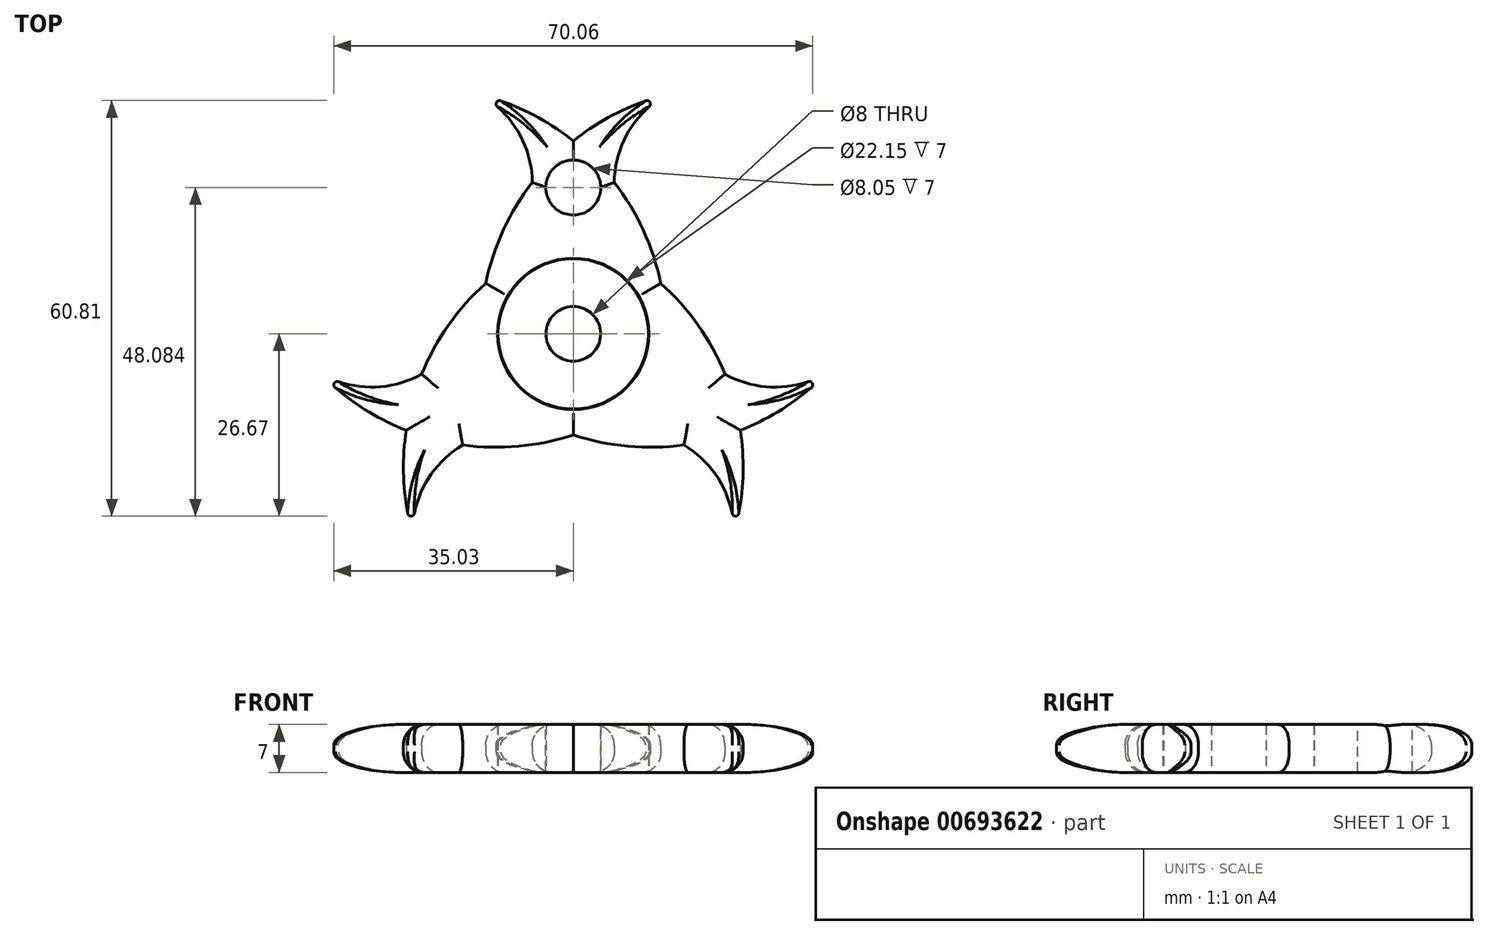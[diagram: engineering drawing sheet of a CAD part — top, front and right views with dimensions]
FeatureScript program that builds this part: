
annotation { "Feature Type Name" : "Feature", "Feature Type Description" : "" }
export const myFeature = defineFeature(function(context is Context, id is Id, definition is map)
    precondition{}
    {
        {
            var Q0;
            Q0=qCreatedBy(makeId("Top.planeOp"),FACE);
            var sketch = newSketch(context, id + "F0", { "sketchPlane" : qUnion([Q0])});
            skCircle(sketch, "E0", {"center": v(0, 0) * mm, "radius": 11.07 * mm});
            skLineSegment(sketch, "E1.bottom", {"start": v(-13.58, 0) * mm, "end": v(13.58, 0) * mm, "construction": true});
            skLineSegment(sketch, "E1.top", {"start": v(-13.58, 35) * mm, "end": v(13.57, 35) * mm, "construction": true});
            skLineSegment(sketch, "E1.left", {"start": v(-13.58, 0) * mm, "end": v(-13.58, 35) * mm, "construction": true});
            skLineSegment(sketch, "E1.right", {"start": v(13.58, 0) * mm, "end": v(13.57, 35) * mm, "construction": true});
            skArc(sketch, "E2", {"start": v(12.81, 7.4) * mm, "mid": v(10.24, 15.16) * mm, "end": v(6, 22.15) * mm});
            skArc(sketch, "E3", {"start": v(13.57, 35) * mm, "mid": v(6.43, 32.33) * mm, "end": v(0, 28.23) * mm});
            skArc(sketch, "E4", {"start": v(-6, 22.15) * mm, "mid": v(-8.07, 29.58) * mm, "end": v(-13.58, 35) * mm});
            skArc(sketch, "E5", {"start": v(13.57, 35) * mm, "mid": v(8.07, 29.58) * mm, "end": v(6, 22.15) * mm});
            skArc(sketch, "E6.trimOffspring", {"start": v(-6, 22.15) * mm, "mid": v(-10.24, 15.16) * mm, "end": v(-12.81, 7.4) * mm});
            skArc(sketch, "E7.trimOffspring", {"start": v(0, 28.23) * mm, "mid": v(-6.43, 32.33) * mm, "end": v(-13.58, 35) * mm});
            skLineSegment(sketch, "E8", {"start": v(0, 28.23) * mm, "end": v(0, 13.58) * mm, "construction": true});
            skArc(sketch, "E9.1.0", {"start": v(-24.45, -14.11) * mm, "mid": v(-24.79, -21.73) * mm, "end": v(-23.52, -29.26) * mm});
            skArc(sketch, "E9.1.1", {"start": v(-16.18, -16.26) * mm, "mid": v(-21.58, -21.78) * mm, "end": v(-23.52, -29.26) * mm});
            skArc(sketch, "E9.1.2", {"start": v(-37.1, -5.74) * mm, "mid": v(-31.22, -10.6) * mm, "end": v(-24.45, -14.11) * mm});
            skArc(sketch, "E9.1.3", {"start": v(-37.1, -5.74) * mm, "mid": v(-29.66, -7.8) * mm, "end": v(-22.18, -5.88) * mm});
            skArc(sketch, "E9.1.4", {"start": v(-12.81, 7.4) * mm, "mid": v(-18.25, 1.29) * mm, "end": v(-22.18, -5.88) * mm});
            skArc(sketch, "E9.1.5", {"start": v(-16.18, -16.26) * mm, "mid": v(-8, -16.45) * mm, "end": v(0, -14.8) * mm});
            skArc(sketch, "E9.2.0", {"start": v(24.45, -14.11) * mm, "mid": v(31.22, -10.6) * mm, "end": v(37.1, -5.74) * mm});
            skArc(sketch, "E9.2.1", {"start": v(22.18, -5.88) * mm, "mid": v(29.66, -7.8) * mm, "end": v(37.1, -5.74) * mm});
            skArc(sketch, "E9.2.2", {"start": v(23.52, -29.26) * mm, "mid": v(24.79, -21.73) * mm, "end": v(24.45, -14.11) * mm});
            skArc(sketch, "E9.2.3", {"start": v(23.52, -29.26) * mm, "mid": v(21.58, -21.78) * mm, "end": v(16.18, -16.26) * mm});
            skArc(sketch, "E9.2.4", {"start": v(0, -14.8) * mm, "mid": v(8, -16.45) * mm, "end": v(16.18, -16.26) * mm});
            skArc(sketch, "E9.2.5", {"start": v(22.18, -5.88) * mm, "mid": v(18.25, 1.29) * mm, "end": v(12.81, 7.4) * mm});
            skPoint(sketch, "E10.orphan", {"position": v(-6.79, 11.76) * mm});
            skPoint(sketch, "E11.orphan", {"position": v(6.79, 11.76) * mm});
            skPoint(sketch, "E12.orphan", {"position": v(6.79, -11.76) * mm});
            skPoint(sketch, "E13.orphan", {"position": v(-6.79, -11.76) * mm});
            skSolve(sketch);
        }
        {
            var Q0;
            Q0 = qSketchRegion(id + "F0", true);
            extrude(context, id + "F1", {"entities" : qUnion([Q0]), "depth" : 7 * mm, "offsetDistance" : 25 * mm});
        }
        {
            var Q0;
            Q0=makeQuery(id+"F1.opExtrude","CAP_EDGE",EDGE,{"disambiguationData":[OSD([sQuery(id+"F0.wireOp",EDGE,"E9.2.5")])],"isStart":false});
            var Q1;
            Q1=makeQuery(id+"F1.opExtrude","CAP_EDGE",EDGE,{"disambiguationData":[OSD([sQuery(id+"F0.wireOp",EDGE,"E2")])],"isStart":false});
            var Q2;
            Q2=makeQuery(id+"F1.opExtrude","CAP_EDGE",EDGE,{"disambiguationData":[OSD([sQuery(id+"F0.wireOp",EDGE,"E5")])],"isStart":false});
            var Q3;
            Q3=makeQuery(id+"F1.opExtrude","CAP_EDGE",EDGE,{"disambiguationData":[OSD([sQuery(id+"F0.wireOp",EDGE,"E3")])],"isStart":false});
            var Q4;
            Q4=makeQuery(id+"F1.opExtrude","CAP_EDGE",EDGE,{"disambiguationData":[OSD([sQuery(id+"F0.wireOp",EDGE,"E7.trimOffspring")])],"isStart":false});
            var Q5;
            Q5=makeQuery(id+"F1.opExtrude","CAP_EDGE",EDGE,{"disambiguationData":[OSD([sQuery(id+"F0.wireOp",EDGE,"E4")])],"isStart":false});
            var Q6;
            Q6=makeQuery(id+"F1.opExtrude","CAP_EDGE",EDGE,{"disambiguationData":[OSD([sQuery(id+"F0.wireOp",EDGE,"E6.trimOffspring")])],"isStart":false});
            var Q7;
            Q7=makeQuery(id+"F1.opExtrude","CAP_EDGE",EDGE,{"disambiguationData":[OSD([sQuery(id+"F0.wireOp",EDGE,"E9.1.4")])],"isStart":false});
            var Q8;
            Q8=makeQuery(id+"F1.opExtrude","CAP_EDGE",EDGE,{"disambiguationData":[OSD([sQuery(id+"F0.wireOp",EDGE,"E9.1.3")])],"isStart":false});
            var Q9;
            Q9=makeQuery(id+"F1.opExtrude","CAP_EDGE",EDGE,{"disambiguationData":[OSD([sQuery(id+"F0.wireOp",EDGE,"E9.1.2")])],"isStart":false});
            var Q10;
            Q10=makeQuery(id+"F1.opExtrude","CAP_EDGE",EDGE,{"disambiguationData":[OSD([sQuery(id+"F0.wireOp",EDGE,"E9.1.0")])],"isStart":true});
            var Q11;
            Q11=makeQuery(id+"F1.opExtrude","CAP_EDGE",EDGE,{"disambiguationData":[OSD([sQuery(id+"F0.wireOp",EDGE,"E9.1.0")])],"isStart":false});
            var Q12;
            Q12=makeQuery(id+"F1.opExtrude","CAP_EDGE",EDGE,{"disambiguationData":[OSD([sQuery(id+"F0.wireOp",EDGE,"E9.1.1")])],"isStart":false});
            var Q13;
            Q13=makeQuery(id+"F1.opExtrude","CAP_EDGE",EDGE,{"disambiguationData":[OSD([sQuery(id+"F0.wireOp",EDGE,"E9.1.5")])],"isStart":false});
            var Q14;
            Q14=makeQuery(id+"F1.opExtrude","CAP_EDGE",EDGE,{"disambiguationData":[OSD([sQuery(id+"F0.wireOp",EDGE,"E9.2.0")])],"isStart":false});
            var Q15;
            Q15=makeQuery(id+"F1.opExtrude","CAP_EDGE",EDGE,{"disambiguationData":[OSD([sQuery(id+"F0.wireOp",EDGE,"E9.2.2")])],"isStart":false});
            var Q16;
            Q16=makeQuery(id+"F1.opExtrude","CAP_EDGE",EDGE,{"disambiguationData":[OSD([sQuery(id+"F0.wireOp",EDGE,"E9.2.3")])],"isStart":false});
            var Q17;
            Q17=makeQuery(id+"F1.opExtrude","CAP_EDGE",EDGE,{"disambiguationData":[OSD([sQuery(id+"F0.wireOp",EDGE,"E9.2.4")])],"isStart":false});
            var Q18;
            Q18=makeQuery(id+"F1.opExtrude","CAP_EDGE",EDGE,{"disambiguationData":[OSD([sQuery(id+"F0.wireOp",EDGE,"E9.2.1")])],"isStart":false});
            var Q19;
            Q19=makeQuery(id+"F1.opExtrude","CAP_EDGE",EDGE,{"disambiguationData":[OSD([sQuery(id+"F0.wireOp",EDGE,"E9.2.0")])],"isStart":true});
            var Q20;
            Q20=makeQuery(id+"F1.opExtrude","CAP_EDGE",EDGE,{"disambiguationData":[OSD([sQuery(id+"F0.wireOp",EDGE,"E9.2.2")])],"isStart":true});
            var Q21;
            Q21=makeQuery(id+"F1.opExtrude","CAP_EDGE",EDGE,{"disambiguationData":[OSD([sQuery(id+"F0.wireOp",EDGE,"E9.2.1")])],"isStart":true});
            var Q22;
            Q22=makeQuery(id+"F1.opExtrude","CAP_EDGE",EDGE,{"disambiguationData":[OSD([sQuery(id+"F0.wireOp",EDGE,"E9.2.5")])],"isStart":true});
            var Q23;
            Q23=makeQuery(id+"F1.opExtrude","CAP_EDGE",EDGE,{"disambiguationData":[OSD([sQuery(id+"F0.wireOp",EDGE,"E2")])],"isStart":true});
            var Q24;
            Q24=makeQuery(id+"F1.opExtrude","CAP_EDGE",EDGE,{"disambiguationData":[OSD([sQuery(id+"F0.wireOp",EDGE,"E5")])],"isStart":true});
            var Q25;
            Q25=makeQuery(id+"F1.opExtrude","CAP_EDGE",EDGE,{"disambiguationData":[OSD([sQuery(id+"F0.wireOp",EDGE,"E3")])],"isStart":true});
            var Q26;
            Q26=makeQuery(id+"F1.opExtrude","CAP_EDGE",EDGE,{"disambiguationData":[OSD([sQuery(id+"F0.wireOp",EDGE,"E7.trimOffspring")])],"isStart":true});
            var Q27;
            Q27=makeQuery(id+"F1.opExtrude","CAP_EDGE",EDGE,{"disambiguationData":[OSD([sQuery(id+"F0.wireOp",EDGE,"E4")])],"isStart":true});
            var Q28;
            Q28=makeQuery(id+"F1.opExtrude","CAP_EDGE",EDGE,{"disambiguationData":[OSD([sQuery(id+"F0.wireOp",EDGE,"E6.trimOffspring")])],"isStart":true});
            var Q29;
            Q29=makeQuery(id+"F1.opExtrude","CAP_EDGE",EDGE,{"disambiguationData":[OSD([sQuery(id+"F0.wireOp",EDGE,"E9.1.4")])],"isStart":true});
            var Q30;
            Q30=makeQuery(id+"F1.opExtrude","CAP_EDGE",EDGE,{"disambiguationData":[OSD([sQuery(id+"F0.wireOp",EDGE,"E9.1.3")])],"isStart":true});
            var Q31;
            Q31=makeQuery(id+"F1.opExtrude","CAP_EDGE",EDGE,{"disambiguationData":[OSD([sQuery(id+"F0.wireOp",EDGE,"E9.1.2")])],"isStart":true});
            var Q32;
            Q32=makeQuery(id+"F1.opExtrude","CAP_EDGE",EDGE,{"disambiguationData":[OSD([sQuery(id+"F0.wireOp",EDGE,"E9.1.1")])],"isStart":true});
            var Q33;
            Q33=makeQuery(id+"F1.opExtrude","CAP_EDGE",EDGE,{"disambiguationData":[OSD([sQuery(id+"F0.wireOp",EDGE,"E9.1.5")])],"isStart":true});
            var Q34;
            Q34=makeQuery(id+"F1.opExtrude","CAP_EDGE",EDGE,{"disambiguationData":[OSD([sQuery(id+"F0.wireOp",EDGE,"E9.2.4")])],"isStart":true});
            var Q35;
            Q35=makeQuery(id+"F1.opExtrude","CAP_EDGE",EDGE,{"disambiguationData":[OSD([sQuery(id+"F0.wireOp",EDGE,"E9.2.3")])],"isStart":true});
            fillet(context, id + "F2", {"entities" : qUnion([Q0, Q1, Q2, Q3, Q4, Q5, Q6, Q7, Q8, Q9, Q10, Q11, Q12, Q13, Q14, Q15, Q16, Q17, Q18, Q19, Q20, Q21, Q22, Q23, Q24, Q25, Q26, Q27, Q28, Q29, Q30, Q31, Q32, Q33, Q34, Q35]), "radius" : 3 * mm, "tangentPropagation" : true, "allowEdgeOverflow" : false});
        }
        {
            var Q0;
            Q0=makeQuery(id+"F1.opExtrude","SWEPT_EDGE",EDGE,{"disambiguationData":[OSD([sQuery(id+"F0.wireOp",EDGE,"E9.1.2"),sQuery(id+"F0.wireOp",EDGE,"E9.1.3")])]});
            var Q1;
            Q1=makeQuery(id+"F1.opExtrude","SWEPT_EDGE",EDGE,{"disambiguationData":[OSD([sQuery(id+"F0.wireOp",EDGE,"E9.1.0"),sQuery(id+"F0.wireOp",EDGE,"E9.1.1")])]});
            var Q2;
            Q2=makeQuery(id+"F1.opExtrude","SWEPT_EDGE",EDGE,{"disambiguationData":[OSD([sQuery(id+"F0.wireOp",EDGE,"E9.2.2"),sQuery(id+"F0.wireOp",EDGE,"E9.2.3")])]});
            var Q3;
            Q3=makeQuery(id+"F1.opExtrude","SWEPT_EDGE",EDGE,{"disambiguationData":[OSD([sQuery(id+"F0.wireOp",EDGE,"E9.2.0"),sQuery(id+"F0.wireOp",EDGE,"E9.2.1")])]});
            var Q4;
            Q4=makeQuery(id+"F1.opExtrude","SWEPT_EDGE",EDGE,{"disambiguationData":[OSD([sQuery(id+"F0.wireOp",EDGE,"E3"),sQuery(id+"F0.wireOp",EDGE,"E5")])]});
            var Q5;
            Q5=makeQuery(id+"F1.opExtrude","SWEPT_EDGE",EDGE,{"disambiguationData":[OSD([sQuery(id+"F0.wireOp",EDGE,"E4"),sQuery(id+"F0.wireOp",EDGE,"E7.trimOffspring")])]});
            fillet(context, id + "F3", {"entities" : qUnion([Q0, Q1, Q2, Q3, Q4, Q5]), "radius" : 0.5 * mm, "tangentPropagation" : true, "allowEdgeOverflow" : false});
        }
        {
            var Q0;
            Q0=makeQuery(id+"F1.opExtrude","CAP_FACE",FACE,{"disambiguationData":[OSD([sQuery(id+"F0.wireOp",EDGE,"E0"),sQuery(id+"F0.wireOp",EDGE,"E2"),sQuery(id+"F0.wireOp",EDGE,"E3"),sQuery(id+"F0.wireOp",EDGE,"E4"),sQuery(id+"F0.wireOp",EDGE,"E5"),sQuery(id+"F0.wireOp",EDGE,"E6.trimOffspring"),sQuery(id+"F0.wireOp",EDGE,"E7.trimOffspring"),sQuery(id+"F0.wireOp",EDGE,"E9.1.0"),sQuery(id+"F0.wireOp",EDGE,"E9.1.1"),sQuery(id+"F0.wireOp",EDGE,"E9.1.2"),sQuery(id+"F0.wireOp",EDGE,"E9.1.3"),sQuery(id+"F0.wireOp",EDGE,"E9.1.4"),sQuery(id+"F0.wireOp",EDGE,"E9.1.5"),sQuery(id+"F0.wireOp",EDGE,"E9.2.0"),sQuery(id+"F0.wireOp",EDGE,"E9.2.1"),sQuery(id+"F0.wireOp",EDGE,"E9.2.2"),sQuery(id+"F0.wireOp",EDGE,"E9.2.3"),sQuery(id+"F0.wireOp",EDGE,"E9.2.4"),sQuery(id+"F0.wireOp",EDGE,"E9.2.5")])],"isStart":false});
            var sketch = newSketch(context, id + "F4", { "sketchPlane" : qUnion([Q0])});
            skLineSegment(sketch, "E14", {"start": v(-3.8, 27.32) * mm, "end": v(10.06, 5.8) * mm, "construction": true});
            skLineSegment(sketch, "E15", {"start": v(-10.06, 5.8) * mm, "end": v(3.8, 27.32) * mm, "construction": true});
            skPoint(sketch, "E16", {"position": v(0, 21.41) * mm});
            skSolve(sketch);
        }
        {
            var Q0;
            Q0=sQuery(id+"F4.wireOp",VERTEX,"E16");
            var Q1;
            Q1=makeQuery(id+"F1.opExtrude","SWEPT_BODY",BODY,{"disambiguationData":[OSD([sQuery(id+"F0.wireOp",EDGE,"E0"),sQuery(id+"F0.wireOp",EDGE,"E2"),sQuery(id+"F0.wireOp",EDGE,"E3"),sQuery(id+"F0.wireOp",EDGE,"E4"),sQuery(id+"F0.wireOp",EDGE,"E5"),sQuery(id+"F0.wireOp",EDGE,"E6.trimOffspring"),sQuery(id+"F0.wireOp",EDGE,"E7.trimOffspring"),sQuery(id+"F0.wireOp",EDGE,"E9.1.0"),sQuery(id+"F0.wireOp",EDGE,"E9.1.1"),sQuery(id+"F0.wireOp",EDGE,"E9.1.2"),sQuery(id+"F0.wireOp",EDGE,"E9.1.3"),sQuery(id+"F0.wireOp",EDGE,"E9.1.4"),sQuery(id+"F0.wireOp",EDGE,"E9.1.5"),sQuery(id+"F0.wireOp",EDGE,"E9.2.0"),sQuery(id+"F0.wireOp",EDGE,"E9.2.1"),sQuery(id+"F0.wireOp",EDGE,"E9.2.2"),sQuery(id+"F0.wireOp",EDGE,"E9.2.3"),sQuery(id+"F0.wireOp",EDGE,"E9.2.4"),sQuery(id+"F0.wireOp",EDGE,"E9.2.5")])]});
            hole(context, id + "F5", {"style" : HoleStyle.SIMPLE, "endStyle" : HoleEndStyle.THROUGH, "holeDiameter" : 8.05 * mm, "majorDiameter" : 5 * mm, "isTappedThrough" : true, "tappedDepth" : 12 * mm, "tapClearance" : 3, "startFromSketch" : true, "locations" : qUnion([Q0]), "scope" : qUnion([Q1])});
        }
        {
            var Q0;
            Q0=qCreatedBy(makeId("Right.planeOp"),FACE);
            var sketch = newSketch(context, id + "F6", { "sketchPlane" : qUnion([Q0])});
            skLineSegment(sketch, "E17", {"start": v(0, 0) * mm, "end": v(0, 24.4) * mm});
            skSolve(sketch);
        }
        {
            var Q0;
            Q0=qCreatedBy(makeId("Top.planeOp"),FACE);
            var sketch = newSketch(context, id + "F7", { "sketchPlane" : qUnion([Q0])});
            skCircle(sketch, "E18", {"center": v(0, 0) * mm, "radius": 11 * mm});
            skCircle(sketch, "E19", {"center": v(0, 0) * mm, "radius": 4 * mm});
            skSolve(sketch);
        }
        {
            var Q0;
            Q0 = qSketchRegion(id + "F7", true);
            extrude(context, id + "F8", {"entities" : qUnion([Q0]), "depth" : 7 * mm, "offsetDistance" : 25 * mm});
        }
    });
